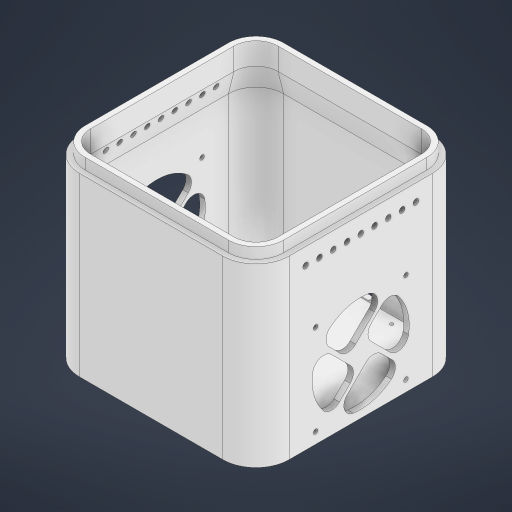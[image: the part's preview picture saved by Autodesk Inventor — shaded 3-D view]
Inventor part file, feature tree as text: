
AUTODESK INVENTOR PART (.ipt)
format: ipt  version: 2024.1 (Build 281209000, 209)  size: 705,536 bytes
history: native  units: mm
features: extrude x13, sketch x9, chamfer x4, projected_geometry x4, fillet x3, other x2
ambient origin geometry x8: Origin, YZ Plane, XZ Plane, XY Plane, X Axis, Y Axis, Z Axis, Center Point
bodies: Body1 (feature_tree)
feature tree (35):
  other  "솔리드1"
  sketch  "스케치1"
  extrude  "돌출1"  Depth=190.0mm
  extrude  "돌출2"  Depth=190.0mm
  sketch  "스케치2"
  extrude  "돌출3"  Depth=30.0mm
  extrude  "돌출4"  Depth=5.0mm
  chamfer  "모따기1"  Distance=160.0mm
  extrude  "돌출5"  Depth=5.0mm TaperAngle=0.0deg
  sketch  "스케치5"
  extrude  "돌출6"  Depth=5.0mm
  extrude  "돌출7"  Depth=10.0mm TaperAngle=0.0deg
  extrude  "돌출8"  Depth=10.0mm TaperAngle=0.0deg
  extrude  "돌출9"  Depth=5.0mm TaperAngle=45.0deg
  sketch  "스케치9"
  extrude  "돌출11"  Depth=30.0mm
  extrude  "돌출12"  Depth=33.5mm
  extrude  "돌출13"  Depth=3.0mm
  chamfer  "모따기2"  Distance=6.0mm
  fillet  "모깎기1"  Radius=50.0mm
  fillet  "모깎기2"  Radius=50.0mm
  chamfer  "모따기3"  Distance=3.3mm
  chamfer  "모따기4"  Distance=3.3mm
  extrude  "돌출14"  Depth=15.1mm
  fillet  "모깎기3"  Radius=35.9mm
  projected_geometry  "투영된 루프1"
  sketch  "스케치4"
  sketch  "스케치6"
  sketch  "스케치7"
  projected_geometry  "투영된 루프2"
  sketch  "스케치10"
  projected_geometry  "투영된 루프3"
  sketch  "스케치11"
  projected_geometry  "투영된 루프4"
  other  "Finish1"
